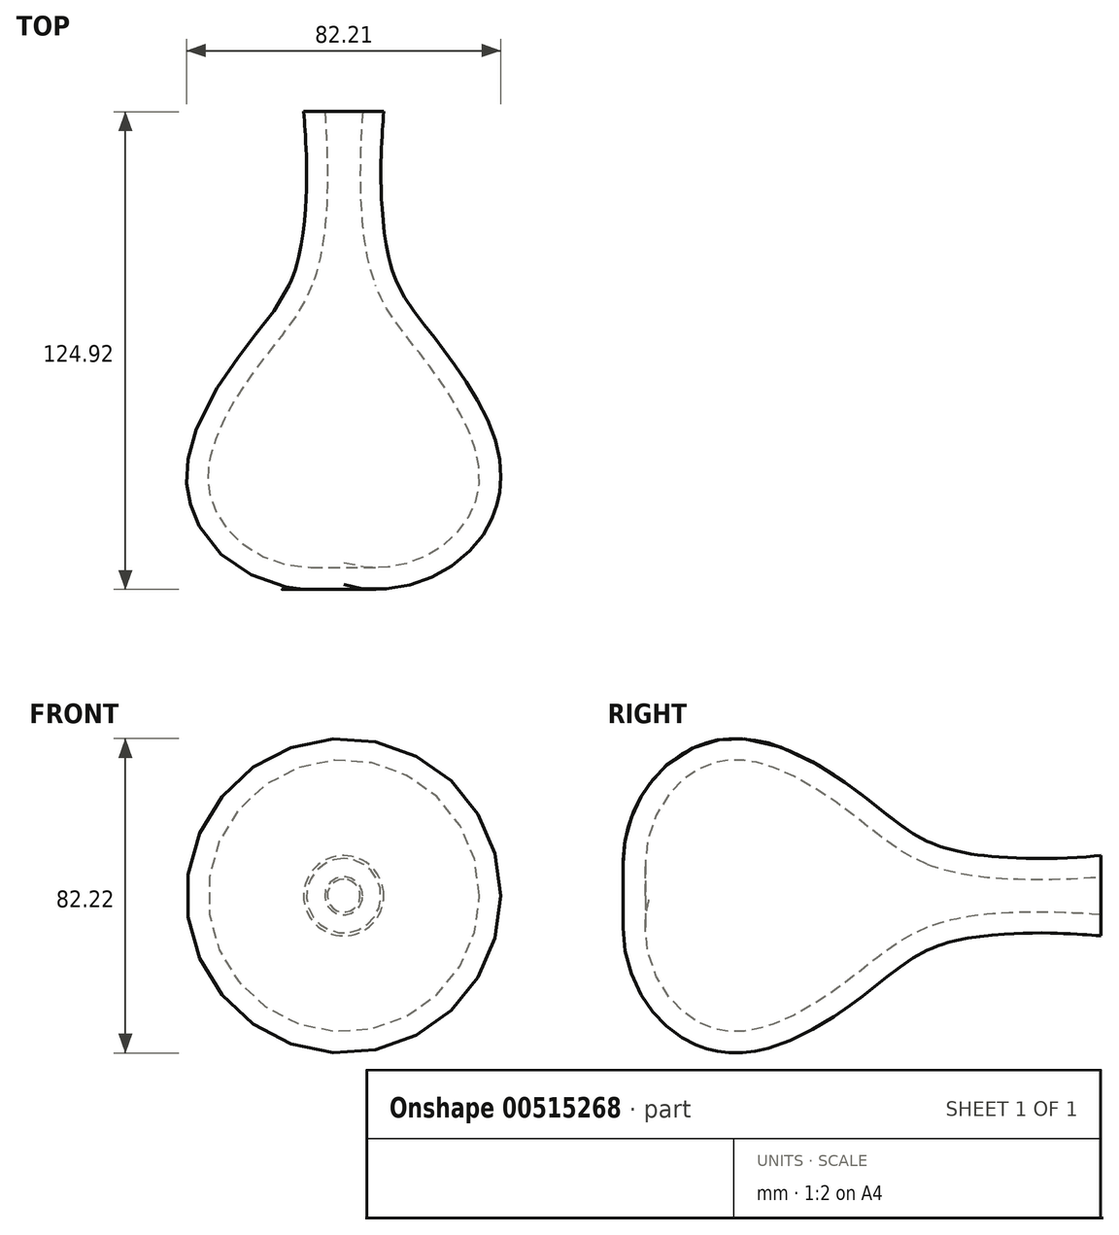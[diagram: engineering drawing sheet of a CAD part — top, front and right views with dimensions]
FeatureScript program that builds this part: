
annotation { "Feature Type Name" : "Feature", "Feature Type Description" : "" }
export const myFeature = defineFeature(function(context is Context, id is Id, definition is map)
    precondition{}
    {
        {
            var Q0;
            Q0=qCreatedBy(makeId("Top.planeOp"),FACE);
            var sketch = newSketch(context, id + "F0", { "sketchPlane" : qUnion([Q0])});
            skLineSegment(sketch, "E0", {"start": v(0, 58.06) * mm, "end": v(0, -58.89) * mm});
            skFitSpline(sketch, "E1", {"points": [v(0, -46.63) * mm, v(35.04, -28.89) * mm, v(20.7, 6.98) * mm, v(8.27, 25.86) * mm, v(5.03, 72.52) * mm], "startDerivative": vector(191.72, -56.97) * mm, "endDerivative": vector(16.7, 227.9) * mm});
            skFitSpline(sketch, "E2", {"points": [v(8.27, 25.86) * mm, v(22.46, 25.86) * mm], "startDerivative": vector(5.97, 0) * mm, "endDerivative": vector(5.97, 0) * mm});
            skFitSpline(sketch, "E3.0", {"points": [v(-1.58, -51.94) * mm, v(0.77, -52.64) * mm, v(5.47, -53.52) * mm, v(12.3, -53.44) * mm, v(18.72, -52.12) * mm, v(24.6, -49.71) * mm, v(29.81, -46.39) * mm, v(34.24, -42.27) * mm, v(37.15, -38.26) * mm, v(38.94, -34.77) * mm, v(39.81, -32.47) * mm, v(40.35, -30.58) * mm, v(40.76, -28.66) * mm, v(41.06, -26.25) * mm, v(41.09, -23.38) * mm, v(40.76, -19.62) * mm, v(39.73, -15.05) * mm, v(37.79, -9.82) * mm, v(35.34, -4.84) * mm, v(32.57, -0.14) * mm, v(29.64, 4.24) * mm, v(27.2, 7.59) * mm, v(25.33, 10.05) * mm, v(23.55, 12.35) * mm, v(21.5, 14.97) * mm, v(19.32, 17.79) * mm, v(17.44, 20.38) * mm, v(15.84, 22.86) * mm, v(14.7, 24.95) * mm, v(13.9, 26.7) * mm, v(13.15, 28.56) * mm, v(12.3, 31.13) * mm, v(11.45, 34.65) * mm, v(10.77, 38.6) * mm, v(10.26, 43.01) * mm, v(9.83, 49.5) * mm, v(9.77, 58.76) * mm, v(10.2, 67.44) * mm, v(10.55, 72.11) * mm]});
            skLineSegment(sketch, "E4", {"start": v(4.94, 71.26) * mm, "end": v(10.49, 71.26) * mm});
            skPoint(sketch, "E5.orphan", {"position": v(0, 71.26) * mm});
            skSolve(sketch);
        }
        {
            var Q0;
            {var subQ5=sQuery(id+"F0.wireOp",EDGE,"E1");Q0=makeQuery(id+"F0.imprint","IMPRINT",FACE,{"disambiguationData":[TD([[makeQuery(id+"F0.imprint","IMPRINT",EDGE,{"derivedFrom":subQ5}),-1.0]])]});}
            var Q1;
            Q1=sQuery(id+"F0.wireOp",EDGE,"E0");
            revolve(context, id + "F1", {"entities" : qUnion([Q0]), "axis" : qUnion([Q1]), "revolveType" : RevolveType.FULL});
        }
    });
